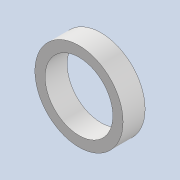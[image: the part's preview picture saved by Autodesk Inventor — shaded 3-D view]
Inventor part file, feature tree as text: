
AUTODESK INVENTOR PART (.ipt)
format: ipt  version: 2020 (Build 240168000, 168)  size: 121,344 bytes
history: native  units: mm
features: other x3, sketch x2, extrude x1, plane x1, revolve x1, fillet x1, reference x1
ambient origin geometry x8: Origin, YZ Plane, XZ Plane, XY Plane, X Axis, Y Axis, Z Axis, Center Point
bodies: Solid1 (feature_tree)
feature tree (10):
  extrude  "Extrusion1"  Depth=8.0mm
  plane  "Work Plane1"
  revolve  "Revolution1"  [1 undecoded]
  fillet  "Fillet1"  Radius=0.5mm
  sketch  "Sketch1"  dims[d0=6.15mm d1=8.0mm]
  reference  "Reference1"
  sketch  "Sketch2"  dims[d2=2.0mm d3=0.0mm d4=0.5mm d5=0.5mm d6=0.5mm d7=90.0deg d8=0.2mm]
  parser-record x1  (decoder bookkeeping rows leaked as tree rows — omitted from the tree; the rows remain in map.json)
  other  "tip_3_ass.iam"
  other  "bearing_3_6_2:4"
note: 1 file-system path scrubbed to <path> (originals preserved in map.json)
note: 1 required parameter value undecoded (feature->parameter linkage not recoverable at this tier; creation-order binding heuristic only, values carry confidence <= 0.55)
